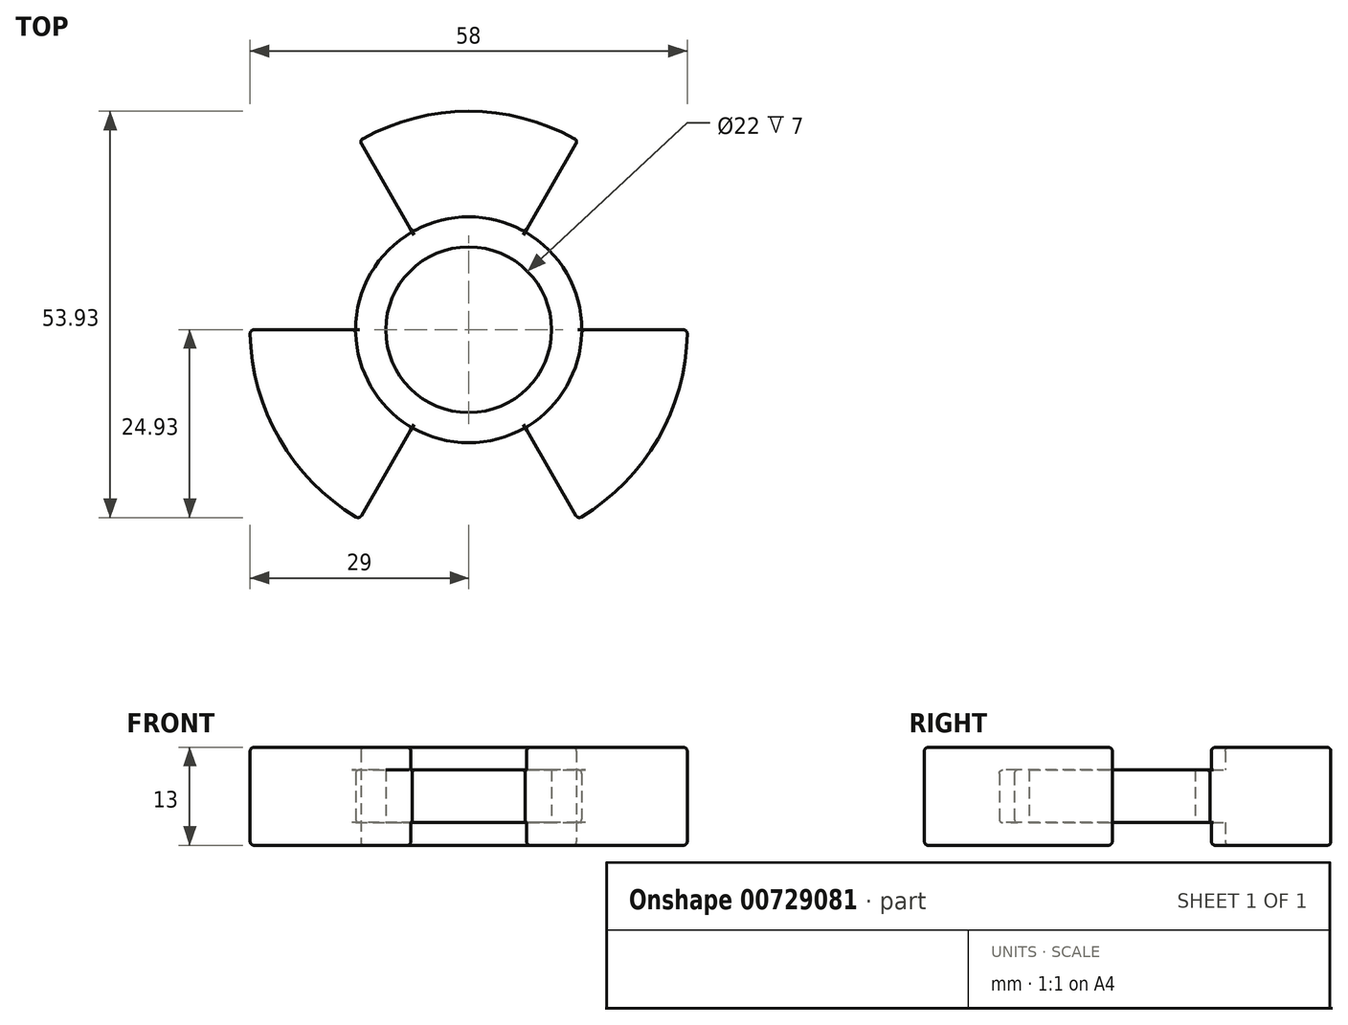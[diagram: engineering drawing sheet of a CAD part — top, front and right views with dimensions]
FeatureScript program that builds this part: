
annotation { "Feature Type Name" : "Feature", "Feature Type Description" : "" }
export const myFeature = defineFeature(function(context is Context, id is Id, definition is map)
    precondition{}
    {
        {
            var Q0;
            Q0=qCreatedBy(makeId("Top.planeOp"),FACE);
            var sketch = newSketch(context, id + "F0", { "sketchPlane" : qUnion([Q0])});
            skCircle(sketch, "E0", {"center": v(0, 0) * mm, "radius": 11 * mm});
            skCircle(sketch, "E1", {"center": v(0, 0) * mm, "radius": 15 * mm});
            skCircle(sketch, "E2", {"center": v(0, 0) * mm, "radius": 29 * mm});
            skLineSegment(sketch, "E3", {"start": v(0, 0) * mm, "end": v(0, 29) * mm});
            skLineSegment(sketch, "E4", {"start": v(0, 0) * mm, "end": v(-14.5, 25.11) * mm});
            skLineSegment(sketch, "E5", {"start": v(0, 0) * mm, "end": v(-29, 0) * mm});
            skLineSegment(sketch, "E6", {"start": v(0, 0) * mm, "end": v(-14.5, -25.11) * mm});
            skLineSegment(sketch, "E7", {"start": v(0, 0) * mm, "end": v(14.5, -25.11) * mm});
            skLineSegment(sketch, "E8", {"start": v(0, 0) * mm, "end": v(14.5, 25.11) * mm});
            skLineSegment(sketch, "E9", {"start": v(0, 0) * mm, "end": v(29, 0) * mm});
            skSolve(sketch);
        }
        {
            var Q0;
            {var subQ0=sQuery(id+"F0.wireOp",EDGE,"E8");var subQ1=sQuery(id+"F0.wireOp",EDGE,"E1");var subQ2=makeQuery(id+"F0.imprint","INTERSECT",VERTEX,{"derivedFrom":[subQ1,subQ0]});Q0=makeQuery(id+"F0.imprint","IMPRINT",FACE,{"disambiguationData":[TD([[makeQuery(id+"F0.imprint","IMPRINT",EDGE,{"disambiguationData":[TD([[subQ2,-1.0]])],"derivedFrom":subQ1}),-1.0]])]});}
            var Q1;
            {var subQ0=sQuery(id+"F0.wireOp",EDGE,"E3");var subQ1=sQuery(id+"F0.wireOp",EDGE,"E1");var subQ2=makeQuery(id+"F0.imprint","INTERSECT",VERTEX,{"derivedFrom":[subQ1,subQ0]});Q1=makeQuery(id+"F0.imprint","IMPRINT",FACE,{"disambiguationData":[TD([[makeQuery(id+"F0.imprint","IMPRINT",EDGE,{"disambiguationData":[TD([[subQ2,-1.0]])],"derivedFrom":subQ1}),-1.0]])]});}
            var Q2;
            {var subQ0=sQuery(id+"F0.wireOp",EDGE,"E5");var subQ1=sQuery(id+"F0.wireOp",EDGE,"E1");var subQ2=makeQuery(id+"F0.imprint","INTERSECT",VERTEX,{"derivedFrom":[subQ1,subQ0]});Q2=makeQuery(id+"F0.imprint","IMPRINT",FACE,{"disambiguationData":[TD([[makeQuery(id+"F0.imprint","IMPRINT",EDGE,{"disambiguationData":[TD([[subQ2,-1.0]])],"derivedFrom":subQ1}),-1.0]])]});}
            var Q3;
            {var subQ0=sQuery(id+"F0.wireOp",EDGE,"E9");var subQ1=sQuery(id+"F0.wireOp",EDGE,"E1");var subQ2=makeQuery(id+"F0.imprint","INTERSECT",VERTEX,{"derivedFrom":[subQ1,subQ0]});Q3=makeQuery(id+"F0.imprint","IMPRINT",FACE,{"disambiguationData":[TD([[makeQuery(id+"F0.imprint","IMPRINT",EDGE,{"disambiguationData":[TD([[subQ2,1.0]])],"derivedFrom":subQ1}),-1.0]])]});}
            extrude(context, id + "F1", {"entities" : qUnion([Q0, Q1, Q2, Q3]), "endBound" : BoundingType.SYMMETRIC, "depth" : 13 * mm, "offsetDistance" : 25 * mm});
        }
        {
            var Q0;
            {var subQ0=sQuery(id+"F0.wireOp",EDGE,"E3");var subQ1=sQuery(id+"F0.wireOp",EDGE,"E0");var subQ2=makeQuery(id+"F0.imprint","INTERSECT",VERTEX,{"derivedFrom":[subQ1,subQ0]});Q0=makeQuery(id+"F0.imprint","IMPRINT",FACE,{"disambiguationData":[TD([[makeQuery(id+"F0.imprint","IMPRINT",EDGE,{"disambiguationData":[TD([[subQ2,-1.0]])],"derivedFrom":subQ1}),-1.0]])]});}
            var Q1;
            {var subQ0=sQuery(id+"F0.wireOp",EDGE,"E8");var subQ1=sQuery(id+"F0.wireOp",EDGE,"E0");var subQ2=makeQuery(id+"F0.imprint","INTERSECT",VERTEX,{"derivedFrom":[subQ1,subQ0]});Q1=makeQuery(id+"F0.imprint","IMPRINT",FACE,{"disambiguationData":[TD([[makeQuery(id+"F0.imprint","IMPRINT",EDGE,{"disambiguationData":[TD([[subQ2,-1.0]])],"derivedFrom":subQ1}),-1.0]])]});}
            var Q2;
            {var subQ0=sQuery(id+"F0.wireOp",EDGE,"E8");var subQ1=sQuery(id+"F0.wireOp",EDGE,"E0");var subQ2=makeQuery(id+"F0.imprint","INTERSECT",VERTEX,{"derivedFrom":[subQ1,subQ0]});Q2=makeQuery(id+"F0.imprint","IMPRINT",FACE,{"disambiguationData":[TD([[makeQuery(id+"F0.imprint","IMPRINT",EDGE,{"disambiguationData":[TD([[subQ2,1.0]])],"derivedFrom":subQ1}),-1.0]])]});}
            var Q3;
            {var subQ0=sQuery(id+"F0.wireOp",EDGE,"E9");var subQ1=sQuery(id+"F0.wireOp",EDGE,"E0");var subQ2=makeQuery(id+"F0.imprint","INTERSECT",VERTEX,{"derivedFrom":[subQ1,subQ0]});Q3=makeQuery(id+"F0.imprint","IMPRINT",FACE,{"disambiguationData":[TD([[makeQuery(id+"F0.imprint","IMPRINT",EDGE,{"disambiguationData":[TD([[subQ2,1.0]])],"derivedFrom":subQ1}),-1.0]])]});}
            var Q4;
            {var subQ0=sQuery(id+"F0.wireOp",EDGE,"E6");var subQ1=sQuery(id+"F0.wireOp",EDGE,"E0");var subQ2=makeQuery(id+"F0.imprint","INTERSECT",VERTEX,{"derivedFrom":[subQ1,subQ0]});Q4=makeQuery(id+"F0.imprint","IMPRINT",FACE,{"disambiguationData":[TD([[makeQuery(id+"F0.imprint","IMPRINT",EDGE,{"disambiguationData":[TD([[subQ2,-1.0]])],"derivedFrom":subQ1}),-1.0]])]});}
            var Q5;
            {var subQ0=sQuery(id+"F0.wireOp",EDGE,"E4");var subQ1=sQuery(id+"F0.wireOp",EDGE,"E0");var subQ2=makeQuery(id+"F0.imprint","INTERSECT",VERTEX,{"derivedFrom":[subQ1,subQ0]});Q5=makeQuery(id+"F0.imprint","IMPRINT",FACE,{"disambiguationData":[TD([[makeQuery(id+"F0.imprint","IMPRINT",EDGE,{"disambiguationData":[TD([[subQ2,-1.0]])],"derivedFrom":subQ1}),-1.0]])]});}
            var Q6;
            {var subQ0=sQuery(id+"F0.wireOp",EDGE,"E5");var subQ1=sQuery(id+"F0.wireOp",EDGE,"E0");var subQ2=makeQuery(id+"F0.imprint","INTERSECT",VERTEX,{"derivedFrom":[subQ1,subQ0]});Q6=makeQuery(id+"F0.imprint","IMPRINT",FACE,{"disambiguationData":[TD([[makeQuery(id+"F0.imprint","IMPRINT",EDGE,{"disambiguationData":[TD([[subQ2,-1.0]])],"derivedFrom":subQ1}),-1.0]])]});}
            extrude(context, id + "F2", {"entities" : qUnion([Q0, Q1, Q2, Q3, Q4, Q5, Q6]), "operationType" : NewBodyOperationType.ADD, "endBound" : BoundingType.SYMMETRIC, "depth" : 7 * mm, "offsetDistance" : 25 * mm});
        }
        {
            var Q0;
            {var subQ0=sQuery(id+"F0.wireOp",EDGE,"E2");var subQ1=makeQuery(id+"F0.imprint","INTERSECT",VERTEX,{"derivedFrom":[subQ0,sQuery(id+"F0.wireOp",EDGE,"E3")]});Q0=makeQuery(id+"F1.opExtrude","CAP_EDGE",EDGE,{"disambiguationData":[OSD([subQ0]),TDD([makeQuery(id+"F0.imprint","IMPRINT",EDGE,{"disambiguationData":[TD([[subQ1,1.0]])],"derivedFrom":subQ0}),makeQuery(id+"F0.imprint","IMPRINT",EDGE,{"disambiguationData":[TD([[subQ1,-1.0]])],"derivedFrom":subQ0})])],"isStart":false});}
            var Q1;
            Q1=makeQuery(id+"F1.opExtrude","CAP_EDGE",EDGE,{"disambiguationData":[OSD([sQuery(id+"F0.wireOp",EDGE,"E4")])],"isStart":false});
            var Q2;
            Q2=makeQuery(id+"F1.opExtrude","CAP_EDGE",EDGE,{"disambiguationData":[OSD([sQuery(id+"F0.wireOp",EDGE,"E8")])],"isStart":false});
            var Q3;
            Q3=makeQuery(id+"F1.opExtrude","SWEPT_EDGE",EDGE,{"disambiguationData":[OSD([sQuery(id+"F0.wireOp",EDGE,"E2"),sQuery(id+"F0.wireOp",EDGE,"E4")])]});
            var Q4;
            Q4=makeQuery(id+"F1.opExtrude","CAP_EDGE",EDGE,{"disambiguationData":[OSD([sQuery(id+"F0.wireOp",EDGE,"E4")])],"isStart":true});
            var Q5;
            {var subQ0=sQuery(id+"F0.wireOp",EDGE,"E2");var subQ1=makeQuery(id+"F0.imprint","INTERSECT",VERTEX,{"derivedFrom":[subQ0,sQuery(id+"F0.wireOp",EDGE,"E3")]});Q5=makeQuery(id+"F1.opExtrude","CAP_EDGE",EDGE,{"disambiguationData":[OSD([subQ0]),TDD([makeQuery(id+"F0.imprint","IMPRINT",EDGE,{"disambiguationData":[TD([[subQ1,1.0]])],"derivedFrom":subQ0}),makeQuery(id+"F0.imprint","IMPRINT",EDGE,{"disambiguationData":[TD([[subQ1,-1.0]])],"derivedFrom":subQ0})])],"isStart":true});}
            var Q6;
            Q6=makeQuery(id+"F1.opExtrude","CAP_EDGE",EDGE,{"disambiguationData":[OSD([sQuery(id+"F0.wireOp",EDGE,"E8")])],"isStart":true});
            var Q7;
            Q7=makeQuery(id+"F1.opExtrude","SWEPT_EDGE",EDGE,{"disambiguationData":[OSD([sQuery(id+"F0.wireOp",EDGE,"E2"),sQuery(id+"F0.wireOp",EDGE,"E8")])]});
            var Q8;
            Q8=makeQuery(id+"F1.opExtrude","SWEPT_EDGE",EDGE,{"disambiguationData":[OSD([sQuery(id+"F0.wireOp",EDGE,"E2"),sQuery(id+"F0.wireOp",EDGE,"E9")])]});
            var Q9;
            {var subQ0=sQuery(id+"F0.wireOp",EDGE,"E2");Q9=makeQuery(id+"F1.opExtrude","CAP_EDGE",EDGE,{"disambiguationData":[OSD([subQ0]),TDD([makeQuery(id+"F0.imprint","IMPRINT",EDGE,{"disambiguationData":[TD([[makeQuery(id+"F0.imprint","INTERSECT",VERTEX,{"derivedFrom":[subQ0,sQuery(id+"F0.wireOp",EDGE,"E7")]}),-1.0]])],"derivedFrom":subQ0})])],"isStart":false});}
            var Q10;
            {var subQ0=sQuery(id+"F0.wireOp",EDGE,"E2");Q10=makeQuery(id+"F1.opExtrude","CAP_EDGE",EDGE,{"disambiguationData":[OSD([subQ0]),TDD([makeQuery(id+"F0.imprint","IMPRINT",EDGE,{"disambiguationData":[TD([[makeQuery(id+"F0.imprint","INTERSECT",VERTEX,{"derivedFrom":[subQ0,sQuery(id+"F0.wireOp",EDGE,"E7")]}),-1.0]])],"derivedFrom":subQ0})])],"isStart":true});}
            var Q11;
            Q11=makeQuery(id+"F1.opExtrude","SWEPT_EDGE",EDGE,{"disambiguationData":[OSD([sQuery(id+"F0.wireOp",EDGE,"E2"),sQuery(id+"F0.wireOp",EDGE,"E7")])]});
            var Q12;
            Q12=makeQuery(id+"F1.opExtrude","CAP_EDGE",EDGE,{"disambiguationData":[OSD([sQuery(id+"F0.wireOp",EDGE,"E6")])],"isStart":true});
            var Q13;
            Q13=makeQuery(id+"F1.opExtrude","CAP_EDGE",EDGE,{"disambiguationData":[OSD([sQuery(id+"F0.wireOp",EDGE,"E7")])],"isStart":true});
            var Q14;
            Q14=makeQuery(id+"F1.opExtrude","CAP_EDGE",EDGE,{"disambiguationData":[OSD([sQuery(id+"F0.wireOp",EDGE,"E7")])],"isStart":false});
            var Q15;
            {var subQ0=sQuery(id+"F0.wireOp",EDGE,"E2");Q15=makeQuery(id+"F1.opExtrude","CAP_EDGE",EDGE,{"disambiguationData":[OSD([subQ0]),TDD([makeQuery(id+"F0.imprint","IMPRINT",EDGE,{"disambiguationData":[TD([[makeQuery(id+"F0.imprint","INTERSECT",VERTEX,{"derivedFrom":[subQ0,sQuery(id+"F0.wireOp",EDGE,"E5")]}),-1.0]])],"derivedFrom":subQ0})])],"isStart":true});}
            var Q16;
            {var subQ0=sQuery(id+"F0.wireOp",EDGE,"E2");Q16=makeQuery(id+"F1.opExtrude","CAP_EDGE",EDGE,{"disambiguationData":[OSD([subQ0]),TDD([makeQuery(id+"F0.imprint","IMPRINT",EDGE,{"disambiguationData":[TD([[makeQuery(id+"F0.imprint","INTERSECT",VERTEX,{"derivedFrom":[subQ0,sQuery(id+"F0.wireOp",EDGE,"E5")]}),-1.0]])],"derivedFrom":subQ0})])],"isStart":false});}
            var Q17;
            Q17=makeQuery(id+"F1.opExtrude","SWEPT_EDGE",EDGE,{"disambiguationData":[OSD([sQuery(id+"F0.wireOp",EDGE,"E2"),sQuery(id+"F0.wireOp",EDGE,"E6")])]});
            var Q18;
            Q18=makeQuery(id+"F1.opExtrude","SWEPT_EDGE",EDGE,{"disambiguationData":[OSD([sQuery(id+"F0.wireOp",EDGE,"E2"),sQuery(id+"F0.wireOp",EDGE,"E5")])]});
            var Q19;
            Q19=makeQuery(id+"F1.opExtrude","CAP_EDGE",EDGE,{"disambiguationData":[OSD([sQuery(id+"F0.wireOp",EDGE,"E5")])],"isStart":false});
            var Q20;
            Q20=makeQuery(id+"F1.opExtrude","CAP_EDGE",EDGE,{"disambiguationData":[OSD([sQuery(id+"F0.wireOp",EDGE,"E5")])],"isStart":true});
            var Q21;
            Q21=makeQuery(id+"F1.opExtrude","CAP_EDGE",EDGE,{"disambiguationData":[OSD([sQuery(id+"F0.wireOp",EDGE,"E9")])],"isStart":true});
            var Q22;
            Q22=makeQuery(id+"F1.opExtrude","CAP_EDGE",EDGE,{"disambiguationData":[OSD([sQuery(id+"F0.wireOp",EDGE,"E9")])],"isStart":false});
            var Q23;
            {var subQ0=sQuery(id+"F0.wireOp",EDGE,"E1");var subQ1=makeQuery(id+"F0.imprint","INTERSECT",VERTEX,{"derivedFrom":[subQ0,sQuery(id+"F0.wireOp",EDGE,"E3")]});Q23=makeQuery(id+"F1.opExtrude","CAP_EDGE",EDGE,{"disambiguationData":[OSD([subQ0]),TDD([makeQuery(id+"F0.imprint","IMPRINT",EDGE,{"disambiguationData":[TD([[makeQuery(id+"F0.imprint","INTERSECT",VERTEX,{"derivedFrom":[subQ0,sQuery(id+"F0.wireOp",EDGE,"E8")]}),-1.0]])],"derivedFrom":subQ0}),makeQuery(id+"F0.imprint","IMPRINT",EDGE,{"disambiguationData":[TD([[subQ1,-1.0]])],"derivedFrom":subQ0})])],"isStart":false});}
            var Q24;
            {var subQ0=sQuery(id+"F0.wireOp",EDGE,"E1");var subQ1=makeQuery(id+"F0.imprint","INTERSECT",VERTEX,{"derivedFrom":[subQ0,sQuery(id+"F0.wireOp",EDGE,"E3")]});Q24=makeQuery(id+"F1.opExtrude","CAP_EDGE",EDGE,{"disambiguationData":[OSD([subQ0]),TDD([makeQuery(id+"F0.imprint","IMPRINT",EDGE,{"disambiguationData":[TD([[makeQuery(id+"F0.imprint","INTERSECT",VERTEX,{"derivedFrom":[subQ0,sQuery(id+"F0.wireOp",EDGE,"E8")]}),-1.0]])],"derivedFrom":subQ0}),makeQuery(id+"F0.imprint","IMPRINT",EDGE,{"disambiguationData":[TD([[subQ1,-1.0]])],"derivedFrom":subQ0})])],"isStart":true});}
            var Q25;
            {var subQ0=sQuery(id+"F0.wireOp",EDGE,"E1");Q25=makeQuery(id+"F1.opExtrude","CAP_EDGE",EDGE,{"disambiguationData":[OSD([subQ0]),TDD([makeQuery(id+"F0.imprint","IMPRINT",EDGE,{"disambiguationData":[TD([[makeQuery(id+"F0.imprint","INTERSECT",VERTEX,{"derivedFrom":[subQ0,sQuery(id+"F0.wireOp",EDGE,"E9")]}),1.0]])],"derivedFrom":subQ0})])],"isStart":true});}
            var Q26;
            {var subQ0=sQuery(id+"F0.wireOp",EDGE,"E1");Q26=makeQuery(id+"F1.opExtrude","CAP_EDGE",EDGE,{"disambiguationData":[OSD([subQ0]),TDD([makeQuery(id+"F0.imprint","IMPRINT",EDGE,{"disambiguationData":[TD([[makeQuery(id+"F0.imprint","INTERSECT",VERTEX,{"derivedFrom":[subQ0,sQuery(id+"F0.wireOp",EDGE,"E5")]}),-1.0]])],"derivedFrom":subQ0})])],"isStart":true});}
            var Q27;
            {var subQ0=sQuery(id+"F0.wireOp",EDGE,"E1");Q27=makeQuery(id+"F1.opExtrude","CAP_EDGE",EDGE,{"disambiguationData":[OSD([subQ0]),TDD([makeQuery(id+"F0.imprint","IMPRINT",EDGE,{"disambiguationData":[TD([[makeQuery(id+"F0.imprint","INTERSECT",VERTEX,{"derivedFrom":[subQ0,sQuery(id+"F0.wireOp",EDGE,"E5")]}),-1.0]])],"derivedFrom":subQ0})])],"isStart":false});}
            var Q28;
            {var subQ0=sQuery(id+"F0.wireOp",EDGE,"E1");Q28=makeQuery(id+"F1.opExtrude","CAP_EDGE",EDGE,{"disambiguationData":[OSD([subQ0]),TDD([makeQuery(id+"F0.imprint","IMPRINT",EDGE,{"disambiguationData":[TD([[makeQuery(id+"F0.imprint","INTERSECT",VERTEX,{"derivedFrom":[subQ0,sQuery(id+"F0.wireOp",EDGE,"E9")]}),1.0]])],"derivedFrom":subQ0})])],"isStart":false});}
            var Q29;
            Q29=makeQuery(id+"F1.opExtrude","CAP_EDGE",EDGE,{"disambiguationData":[OSD([sQuery(id+"F0.wireOp",EDGE,"E6")])],"isStart":false});
            fillet(context, id + "F3", {"entities" : qUnion([Q0, Q1, Q2, Q3, Q4, Q5, Q6, Q7, Q8, Q9, Q10, Q11, Q12, Q13, Q14, Q15, Q16, Q17, Q18, Q19, Q20, Q21, Q22, Q23, Q24, Q25, Q26, Q27, Q28, Q29]), "radius" : 0.5 * mm, "tangentPropagation" : true, "allowEdgeOverflow" : false});
        }
        {
            var Q0;
            {var subQ1=sQuery(id+"F0.wireOp",EDGE,"E5");var subQ2=sQuery(id+"F0.wireOp",EDGE,"E1");var subQ3=makeQuery(id+"F1.opExtrude","SWEPT_FACE",FACE,{"disambiguationData":[OSD([subQ1])]});var subQ4=makeQuery(id+"F1.opExtrude","SWEPT_FACE",FACE,{"disambiguationData":[OSD([subQ2]),TDD([makeQuery(id+"F0.imprint","IMPRINT",EDGE,{"disambiguationData":[TD([[makeQuery(id+"F0.imprint","INTERSECT",VERTEX,{"derivedFrom":[subQ2,subQ1]}),-1.0]])],"derivedFrom":subQ2})])]});Q0=makeQuery(id+"F2.boolean.opBoolean","SPLIT",EDGE,{"disambiguationData":[topologyDisambiguationEdgeConnected([subQ4,subQ3]),TD([makeQuery(id+"F2.opExtrude","CAP_FACE",FACE,{"disambiguationData":[OSD([sQuery(id+"F0.wireOp",EDGE,"E0"),subQ2])],"isStart":false})])],"derivedFrom":makeQuery(id+"F1.opExtrude","SWEPT_EDGE",EDGE,{"disambiguationData":[OSD([subQ2,subQ1])]})});}
            var Q1;
            {var subQ0=sQuery(id+"F0.wireOp",EDGE,"E1");var subQ2=sQuery(id+"F0.wireOp",EDGE,"E5");var subQ3=makeQuery(id+"F1.opExtrude","SWEPT_FACE",FACE,{"disambiguationData":[OSD([subQ2])]});var subQ4=makeQuery(id+"F1.opExtrude","SWEPT_FACE",FACE,{"disambiguationData":[OSD([subQ0]),TDD([makeQuery(id+"F0.imprint","IMPRINT",EDGE,{"disambiguationData":[TD([[makeQuery(id+"F0.imprint","INTERSECT",VERTEX,{"derivedFrom":[subQ0,subQ2]}),-1.0]])],"derivedFrom":subQ0})])]});Q1=makeQuery(id+"F2.boolean.opBoolean","SPLIT",EDGE,{"disambiguationData":[topologyDisambiguationEdgeConnected([subQ4,subQ3]),TD([makeQuery(id+"F2.opExtrude","CAP_FACE",FACE,{"disambiguationData":[OSD([sQuery(id+"F0.wireOp",EDGE,"E0"),subQ0])],"isStart":true})])],"derivedFrom":makeQuery(id+"F1.opExtrude","SWEPT_EDGE",EDGE,{"disambiguationData":[OSD([subQ0,subQ2])]})});}
            var Q2;
            {var subQ0=sQuery(id+"F0.wireOp",EDGE,"E1");var subQ1=sQuery(id+"F0.wireOp",EDGE,"E4");var subQ2=makeQuery(id+"F1.opExtrude","SWEPT_FACE",FACE,{"disambiguationData":[OSD([subQ1])]});var subQ3=sQuery(id+"F0.wireOp",EDGE,"E8");var subQ4=makeQuery(id+"F0.imprint","INTERSECT",VERTEX,{"derivedFrom":[subQ0,sQuery(id+"F0.wireOp",EDGE,"E3")]});var subQ5=makeQuery(id+"F1.opExtrude","SWEPT_FACE",FACE,{"disambiguationData":[OSD([subQ0]),TDD([makeQuery(id+"F0.imprint","IMPRINT",EDGE,{"disambiguationData":[TD([[makeQuery(id+"F0.imprint","INTERSECT",VERTEX,{"derivedFrom":[subQ0,subQ3]}),-1.0]])],"derivedFrom":subQ0}),makeQuery(id+"F0.imprint","IMPRINT",EDGE,{"disambiguationData":[TD([[subQ4,-1.0]])],"derivedFrom":subQ0})])]});Q2=makeQuery(id+"F2.boolean.opBoolean","SPLIT",EDGE,{"disambiguationData":[topologyDisambiguationEdgeConnected([subQ5,subQ2]),TD([makeQuery(id+"F2.opExtrude","CAP_FACE",FACE,{"disambiguationData":[OSD([sQuery(id+"F0.wireOp",EDGE,"E0"),subQ0])],"isStart":false})])],"derivedFrom":makeQuery(id+"F1.opExtrude","SWEPT_EDGE",EDGE,{"disambiguationData":[OSD([subQ0,subQ1])]})});}
            var Q3;
            {var subQ0=sQuery(id+"F0.wireOp",EDGE,"E1");var subQ1=sQuery(id+"F0.wireOp",EDGE,"E4");var subQ2=makeQuery(id+"F1.opExtrude","SWEPT_FACE",FACE,{"disambiguationData":[OSD([subQ1])]});var subQ3=sQuery(id+"F0.wireOp",EDGE,"E8");var subQ4=makeQuery(id+"F0.imprint","INTERSECT",VERTEX,{"derivedFrom":[subQ0,sQuery(id+"F0.wireOp",EDGE,"E3")]});var subQ5=makeQuery(id+"F1.opExtrude","SWEPT_FACE",FACE,{"disambiguationData":[OSD([subQ0]),TDD([makeQuery(id+"F0.imprint","IMPRINT",EDGE,{"disambiguationData":[TD([[makeQuery(id+"F0.imprint","INTERSECT",VERTEX,{"derivedFrom":[subQ0,subQ3]}),-1.0]])],"derivedFrom":subQ0}),makeQuery(id+"F0.imprint","IMPRINT",EDGE,{"disambiguationData":[TD([[subQ4,-1.0]])],"derivedFrom":subQ0})])]});Q3=makeQuery(id+"F2.boolean.opBoolean","SPLIT",EDGE,{"disambiguationData":[topologyDisambiguationEdgeConnected([subQ5,subQ2]),TD([makeQuery(id+"F2.opExtrude","CAP_FACE",FACE,{"disambiguationData":[OSD([sQuery(id+"F0.wireOp",EDGE,"E0"),subQ0])],"isStart":true})])],"derivedFrom":makeQuery(id+"F1.opExtrude","SWEPT_EDGE",EDGE,{"disambiguationData":[OSD([subQ0,subQ1])]})});}
            var Q4;
            {var subQ0=sQuery(id+"F0.wireOp",EDGE,"E1");var subQ1=sQuery(id+"F0.wireOp",EDGE,"E6");var subQ2=makeQuery(id+"F1.opExtrude","SWEPT_FACE",FACE,{"disambiguationData":[OSD([subQ1])]});var subQ3=sQuery(id+"F0.wireOp",EDGE,"E5");var subQ4=makeQuery(id+"F1.opExtrude","SWEPT_FACE",FACE,{"disambiguationData":[OSD([subQ0]),TDD([makeQuery(id+"F0.imprint","IMPRINT",EDGE,{"disambiguationData":[TD([[makeQuery(id+"F0.imprint","INTERSECT",VERTEX,{"derivedFrom":[subQ0,subQ3]}),-1.0]])],"derivedFrom":subQ0})])]});Q4=makeQuery(id+"F2.boolean.opBoolean","SPLIT",EDGE,{"disambiguationData":[topologyDisambiguationEdgeConnected([subQ4,subQ2]),TD([makeQuery(id+"F2.opExtrude","CAP_FACE",FACE,{"disambiguationData":[OSD([sQuery(id+"F0.wireOp",EDGE,"E0"),subQ0])],"isStart":true})])],"derivedFrom":makeQuery(id+"F1.opExtrude","SWEPT_EDGE",EDGE,{"disambiguationData":[OSD([subQ0,subQ1])]})});}
            var Q5;
            {var subQ0=sQuery(id+"F0.wireOp",EDGE,"E6");var subQ1=makeQuery(id+"F1.opExtrude","SWEPT_FACE",FACE,{"disambiguationData":[OSD([subQ0])]});var subQ2=sQuery(id+"F0.wireOp",EDGE,"E5");var subQ3=sQuery(id+"F0.wireOp",EDGE,"E1");var subQ4=makeQuery(id+"F1.opExtrude","SWEPT_FACE",FACE,{"disambiguationData":[OSD([subQ3]),TDD([makeQuery(id+"F0.imprint","IMPRINT",EDGE,{"disambiguationData":[TD([[makeQuery(id+"F0.imprint","INTERSECT",VERTEX,{"derivedFrom":[subQ3,subQ2]}),-1.0]])],"derivedFrom":subQ3})])]});Q5=makeQuery(id+"F2.boolean.opBoolean","SPLIT",EDGE,{"disambiguationData":[topologyDisambiguationEdgeConnected([subQ4,subQ1]),TD([makeQuery(id+"F2.opExtrude","CAP_FACE",FACE,{"disambiguationData":[OSD([sQuery(id+"F0.wireOp",EDGE,"E0"),subQ3])],"isStart":false})])],"derivedFrom":makeQuery(id+"F1.opExtrude","SWEPT_EDGE",EDGE,{"disambiguationData":[OSD([subQ3,subQ0])]})});}
            var Q6;
            {var subQ0=sQuery(id+"F0.wireOp",EDGE,"E7");var subQ1=makeQuery(id+"F1.opExtrude","SWEPT_FACE",FACE,{"disambiguationData":[OSD([subQ0])]});var subQ2=sQuery(id+"F0.wireOp",EDGE,"E1");var subQ3=sQuery(id+"F0.wireOp",EDGE,"E9");var subQ4=makeQuery(id+"F1.opExtrude","SWEPT_FACE",FACE,{"disambiguationData":[OSD([subQ2]),TDD([makeQuery(id+"F0.imprint","IMPRINT",EDGE,{"disambiguationData":[TD([[makeQuery(id+"F0.imprint","INTERSECT",VERTEX,{"derivedFrom":[subQ2,subQ3]}),1.0]])],"derivedFrom":subQ2})])]});Q6=makeQuery(id+"F2.boolean.opBoolean","SPLIT",EDGE,{"disambiguationData":[topologyDisambiguationEdgeConnected([subQ4,subQ1]),TD([makeQuery(id+"F2.opExtrude","CAP_FACE",FACE,{"disambiguationData":[OSD([sQuery(id+"F0.wireOp",EDGE,"E0"),subQ2])],"isStart":false})])],"derivedFrom":makeQuery(id+"F1.opExtrude","SWEPT_EDGE",EDGE,{"disambiguationData":[OSD([subQ2,subQ0])]})});}
            var Q7;
            {var subQ0=sQuery(id+"F0.wireOp",EDGE,"E7");var subQ1=makeQuery(id+"F1.opExtrude","SWEPT_FACE",FACE,{"disambiguationData":[OSD([subQ0])]});var subQ2=sQuery(id+"F0.wireOp",EDGE,"E1");var subQ3=sQuery(id+"F0.wireOp",EDGE,"E9");var subQ4=makeQuery(id+"F1.opExtrude","SWEPT_FACE",FACE,{"disambiguationData":[OSD([subQ2]),TDD([makeQuery(id+"F0.imprint","IMPRINT",EDGE,{"disambiguationData":[TD([[makeQuery(id+"F0.imprint","INTERSECT",VERTEX,{"derivedFrom":[subQ2,subQ3]}),1.0]])],"derivedFrom":subQ2})])]});Q7=makeQuery(id+"F2.boolean.opBoolean","SPLIT",EDGE,{"disambiguationData":[topologyDisambiguationEdgeConnected([subQ4,subQ1]),TD([makeQuery(id+"F2.opExtrude","CAP_FACE",FACE,{"disambiguationData":[OSD([sQuery(id+"F0.wireOp",EDGE,"E0"),subQ2])],"isStart":true})])],"derivedFrom":makeQuery(id+"F1.opExtrude","SWEPT_EDGE",EDGE,{"disambiguationData":[OSD([subQ2,subQ0])]})});}
            var Q8;
            {var subQ0=sQuery(id+"F0.wireOp",EDGE,"E9");var subQ1=makeQuery(id+"F1.opExtrude","SWEPT_FACE",FACE,{"disambiguationData":[OSD([subQ0])]});var subQ2=sQuery(id+"F0.wireOp",EDGE,"E1");var subQ4=makeQuery(id+"F1.opExtrude","SWEPT_FACE",FACE,{"disambiguationData":[OSD([subQ2]),TDD([makeQuery(id+"F0.imprint","IMPRINT",EDGE,{"disambiguationData":[TD([[makeQuery(id+"F0.imprint","INTERSECT",VERTEX,{"derivedFrom":[subQ2,subQ0]}),1.0]])],"derivedFrom":subQ2})])]});Q8=makeQuery(id+"F2.boolean.opBoolean","SPLIT",EDGE,{"disambiguationData":[topologyDisambiguationEdgeConnected([subQ4,subQ1]),TD([makeQuery(id+"F2.opExtrude","CAP_FACE",FACE,{"disambiguationData":[OSD([sQuery(id+"F0.wireOp",EDGE,"E0"),subQ2])],"isStart":false})])],"derivedFrom":makeQuery(id+"F1.opExtrude","SWEPT_EDGE",EDGE,{"disambiguationData":[OSD([subQ2,subQ0])]})});}
            var Q9;
            {var subQ0=sQuery(id+"F0.wireOp",EDGE,"E1");var subQ1=sQuery(id+"F0.wireOp",EDGE,"E9");var subQ2=makeQuery(id+"F1.opExtrude","SWEPT_FACE",FACE,{"disambiguationData":[OSD([subQ1])]});var subQ4=makeQuery(id+"F1.opExtrude","SWEPT_FACE",FACE,{"disambiguationData":[OSD([subQ0]),TDD([makeQuery(id+"F0.imprint","IMPRINT",EDGE,{"disambiguationData":[TD([[makeQuery(id+"F0.imprint","INTERSECT",VERTEX,{"derivedFrom":[subQ0,subQ1]}),1.0]])],"derivedFrom":subQ0})])]});Q9=makeQuery(id+"F2.boolean.opBoolean","SPLIT",EDGE,{"disambiguationData":[topologyDisambiguationEdgeConnected([subQ4,subQ2]),TD([makeQuery(id+"F2.opExtrude","CAP_FACE",FACE,{"disambiguationData":[OSD([sQuery(id+"F0.wireOp",EDGE,"E0"),subQ0])],"isStart":true})])],"derivedFrom":makeQuery(id+"F1.opExtrude","SWEPT_EDGE",EDGE,{"disambiguationData":[OSD([subQ0,subQ1])]})});}
            var Q10;
            {var subQ0=sQuery(id+"F0.wireOp",EDGE,"E1");var subQ1=sQuery(id+"F0.wireOp",EDGE,"E8");var subQ2=makeQuery(id+"F1.opExtrude","SWEPT_FACE",FACE,{"disambiguationData":[OSD([subQ1])]});var subQ4=makeQuery(id+"F0.imprint","INTERSECT",VERTEX,{"derivedFrom":[subQ0,sQuery(id+"F0.wireOp",EDGE,"E3")]});var subQ5=makeQuery(id+"F1.opExtrude","SWEPT_FACE",FACE,{"disambiguationData":[OSD([subQ0]),TDD([makeQuery(id+"F0.imprint","IMPRINT",EDGE,{"disambiguationData":[TD([[makeQuery(id+"F0.imprint","INTERSECT",VERTEX,{"derivedFrom":[subQ0,subQ1]}),-1.0]])],"derivedFrom":subQ0}),makeQuery(id+"F0.imprint","IMPRINT",EDGE,{"disambiguationData":[TD([[subQ4,-1.0]])],"derivedFrom":subQ0})])]});Q10=makeQuery(id+"F2.boolean.opBoolean","SPLIT",EDGE,{"disambiguationData":[topologyDisambiguationEdgeConnected([subQ5,subQ2]),TD([makeQuery(id+"F2.opExtrude","CAP_FACE",FACE,{"disambiguationData":[OSD([sQuery(id+"F0.wireOp",EDGE,"E0"),subQ0])],"isStart":false})])],"derivedFrom":makeQuery(id+"F1.opExtrude","SWEPT_EDGE",EDGE,{"disambiguationData":[OSD([subQ0,subQ1])]})});}
            var Q11;
            {var subQ0=sQuery(id+"F0.wireOp",EDGE,"E1");var subQ1=sQuery(id+"F0.wireOp",EDGE,"E8");var subQ2=makeQuery(id+"F1.opExtrude","SWEPT_FACE",FACE,{"disambiguationData":[OSD([subQ1])]});var subQ4=makeQuery(id+"F0.imprint","INTERSECT",VERTEX,{"derivedFrom":[subQ0,sQuery(id+"F0.wireOp",EDGE,"E3")]});var subQ5=makeQuery(id+"F1.opExtrude","SWEPT_FACE",FACE,{"disambiguationData":[OSD([subQ0]),TDD([makeQuery(id+"F0.imprint","IMPRINT",EDGE,{"disambiguationData":[TD([[makeQuery(id+"F0.imprint","INTERSECT",VERTEX,{"derivedFrom":[subQ0,subQ1]}),-1.0]])],"derivedFrom":subQ0}),makeQuery(id+"F0.imprint","IMPRINT",EDGE,{"disambiguationData":[TD([[subQ4,-1.0]])],"derivedFrom":subQ0})])]});Q11=makeQuery(id+"F2.boolean.opBoolean","SPLIT",EDGE,{"disambiguationData":[topologyDisambiguationEdgeConnected([subQ5,subQ2]),TD([makeQuery(id+"F2.opExtrude","CAP_FACE",FACE,{"disambiguationData":[OSD([sQuery(id+"F0.wireOp",EDGE,"E0"),subQ0])],"isStart":true})])],"derivedFrom":makeQuery(id+"F1.opExtrude","SWEPT_EDGE",EDGE,{"disambiguationData":[OSD([subQ0,subQ1])]})});}
            fillet(context, id + "F4", {"entities" : qUnion([Q0, Q1, Q2, Q3, Q4, Q5, Q6, Q7, Q8, Q9, Q10, Q11]), "radius" : .5 * mm, "tangentPropagation" : true, "allowEdgeOverflow" : false});
        }
        {
            var Q0;
            {var subQ1=sQuery(id+"F0.wireOp",EDGE,"E1");var subQ2=sQuery(id+"F0.wireOp",EDGE,"E8");var subQ3=makeQuery(id+"F2.opExtrude","CAP_FACE",FACE,{"disambiguationData":[OSD([sQuery(id+"F0.wireOp",EDGE,"E0"),subQ1])],"isStart":true});var subQ5=makeQuery(id+"F2.opExtrude","SWEPT_FACE",FACE,{"disambiguationData":[OSD([subQ1])]});Q0=makeQuery(id+"F2.boolean.opBoolean","SPLIT",EDGE,{"disambiguationData":[topologyDisambiguationEdgeConnected([subQ3,subQ5]),TD([makeQuery(id+"F1.opExtrude","SWEPT_FACE",FACE,{"disambiguationData":[OSD([subQ2])]})])],"derivedFrom":makeQuery(id+"F2.opExtrude","CAP_EDGE",EDGE,{"disambiguationData":[OSD([subQ1])],"isStart":true})});}
            var Q1;
            {var subQ1=sQuery(id+"F0.wireOp",EDGE,"E1");var subQ2=makeQuery(id+"F2.opExtrude","CAP_FACE",FACE,{"disambiguationData":[OSD([sQuery(id+"F0.wireOp",EDGE,"E0"),subQ1])],"isStart":false});var subQ3=sQuery(id+"F0.wireOp",EDGE,"E8");var subQ5=makeQuery(id+"F2.opExtrude","SWEPT_FACE",FACE,{"disambiguationData":[OSD([subQ1])]});Q1=makeQuery(id+"F2.boolean.opBoolean","SPLIT",EDGE,{"disambiguationData":[topologyDisambiguationEdgeConnected([subQ2,subQ5]),TD([makeQuery(id+"F1.opExtrude","SWEPT_FACE",FACE,{"disambiguationData":[OSD([subQ3])]})])],"derivedFrom":makeQuery(id+"F2.opExtrude","CAP_EDGE",EDGE,{"disambiguationData":[OSD([subQ1])],"isStart":false})});}
            var Q2;
            {var subQ0=sQuery(id+"F0.wireOp",EDGE,"E4");var subQ2=sQuery(id+"F0.wireOp",EDGE,"E1");var subQ4=makeQuery(id+"F2.opExtrude","CAP_FACE",FACE,{"disambiguationData":[OSD([sQuery(id+"F0.wireOp",EDGE,"E0"),subQ2])],"isStart":false});var subQ5=makeQuery(id+"F2.opExtrude","SWEPT_FACE",FACE,{"disambiguationData":[OSD([subQ2])]});Q2=makeQuery(id+"F2.boolean.opBoolean","SPLIT",EDGE,{"disambiguationData":[topologyDisambiguationEdgeConnected([subQ4,subQ5]),TD([makeQuery(id+"F1.opExtrude","SWEPT_FACE",FACE,{"disambiguationData":[OSD([subQ0])]})])],"derivedFrom":makeQuery(id+"F2.opExtrude","CAP_EDGE",EDGE,{"disambiguationData":[OSD([subQ2])],"isStart":false})});}
            var Q3;
            {var subQ1=sQuery(id+"F0.wireOp",EDGE,"E6");var subQ2=sQuery(id+"F0.wireOp",EDGE,"E1");var subQ3=makeQuery(id+"F2.opExtrude","CAP_FACE",FACE,{"disambiguationData":[OSD([sQuery(id+"F0.wireOp",EDGE,"E0"),subQ2])],"isStart":false});var subQ4=makeQuery(id+"F2.opExtrude","SWEPT_FACE",FACE,{"disambiguationData":[OSD([subQ2])]});Q3=makeQuery(id+"F2.boolean.opBoolean","SPLIT",EDGE,{"disambiguationData":[topologyDisambiguationEdgeConnected([subQ3,subQ4]),TD([makeQuery(id+"F1.opExtrude","SWEPT_FACE",FACE,{"disambiguationData":[OSD([subQ1])]})])],"derivedFrom":makeQuery(id+"F2.opExtrude","CAP_EDGE",EDGE,{"disambiguationData":[OSD([subQ2])],"isStart":false})});}
            var Q4;
            {var subQ0=sQuery(id+"F0.wireOp",EDGE,"E4");var subQ2=sQuery(id+"F0.wireOp",EDGE,"E1");var subQ4=makeQuery(id+"F2.opExtrude","CAP_FACE",FACE,{"disambiguationData":[OSD([sQuery(id+"F0.wireOp",EDGE,"E0"),subQ2])],"isStart":true});var subQ5=makeQuery(id+"F2.opExtrude","SWEPT_FACE",FACE,{"disambiguationData":[OSD([subQ2])]});Q4=makeQuery(id+"F2.boolean.opBoolean","SPLIT",EDGE,{"disambiguationData":[topologyDisambiguationEdgeConnected([subQ4,subQ5]),TD([makeQuery(id+"F1.opExtrude","SWEPT_FACE",FACE,{"disambiguationData":[OSD([subQ0])]})])],"derivedFrom":makeQuery(id+"F2.opExtrude","CAP_EDGE",EDGE,{"disambiguationData":[OSD([subQ2])],"isStart":true})});}
            var Q5;
            {var subQ1=sQuery(id+"F0.wireOp",EDGE,"E6");var subQ2=sQuery(id+"F0.wireOp",EDGE,"E1");var subQ3=makeQuery(id+"F2.opExtrude","CAP_FACE",FACE,{"disambiguationData":[OSD([sQuery(id+"F0.wireOp",EDGE,"E0"),subQ2])],"isStart":true});var subQ4=makeQuery(id+"F2.opExtrude","SWEPT_FACE",FACE,{"disambiguationData":[OSD([subQ2])]});Q5=makeQuery(id+"F2.boolean.opBoolean","SPLIT",EDGE,{"disambiguationData":[topologyDisambiguationEdgeConnected([subQ3,subQ4]),TD([makeQuery(id+"F1.opExtrude","SWEPT_FACE",FACE,{"disambiguationData":[OSD([subQ1])]})])],"derivedFrom":makeQuery(id+"F2.opExtrude","CAP_EDGE",EDGE,{"disambiguationData":[OSD([subQ2])],"isStart":true})});}
            fillet(context, id + "F5", {"entities" : qUnion([Q0, Q1, Q2, Q3, Q4, Q5]), "radius" : .5 * mm, "tangentPropagation" : true, "allowEdgeOverflow" : false});
        }
    });
